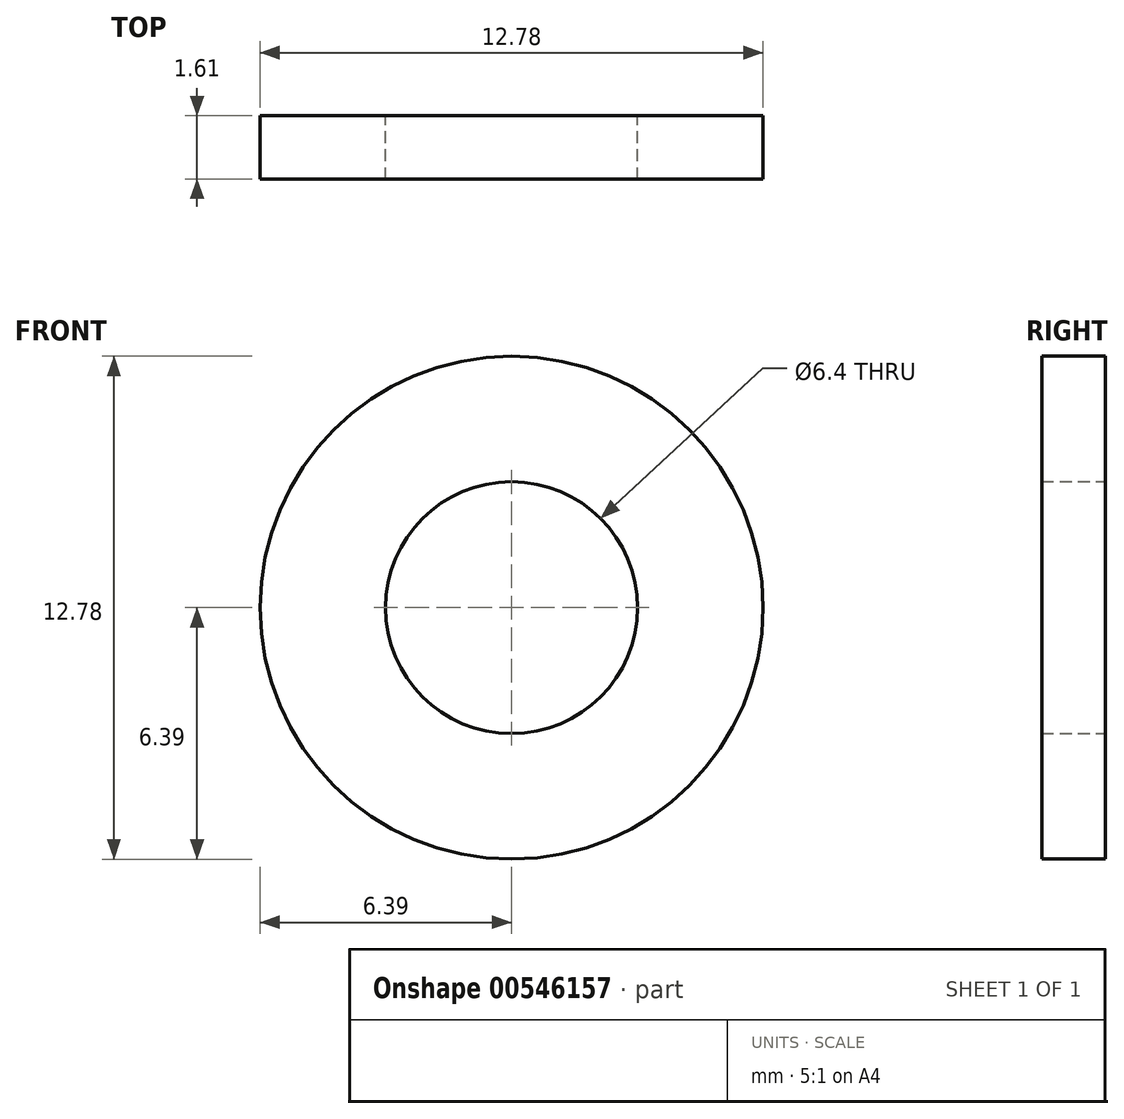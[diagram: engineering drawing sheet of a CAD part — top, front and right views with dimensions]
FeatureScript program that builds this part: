
annotation { "Feature Type Name" : "Feature", "Feature Type Description" : "" }
export const myFeature = defineFeature(function(context is Context, id is Id, definition is map)
    precondition{}
    {
        {
            var Q0;
            Q0=qCreatedBy(makeId("Front.planeOp"),FACE);
            var sketch = newSketch(context, id + "F0", { "sketchPlane" : qUnion([Q0])});
            skCircle(sketch, "E0", {"center": v(0, 0) * mm, "radius": 6.39 * mm});
            skCircle(sketch, "E1", {"center": v(0, 0) * mm, "radius": 3.2 * mm});
            skPoint(sketch, "E2.center.orphan", {"position": v(-13.7, 0) * mm});
            skSolve(sketch);
        }
        {
            var Q0;
            Q0=makeQuery(id+"F0.imprint","IMPRINT",FACE,{"disambiguationData":[TD([[makeQuery(id+"F0.imprint","IMPRINT",EDGE,{"derivedFrom":sQuery(id+"F0.wireOp",EDGE,"E0")}),1.0]])]});
            extrude(context, id + "F1", {"entities" : qUnion([Q0]), "depth" : 1.61 * mm, "offsetDistance" : 25.4 * mm});
        }
    });
